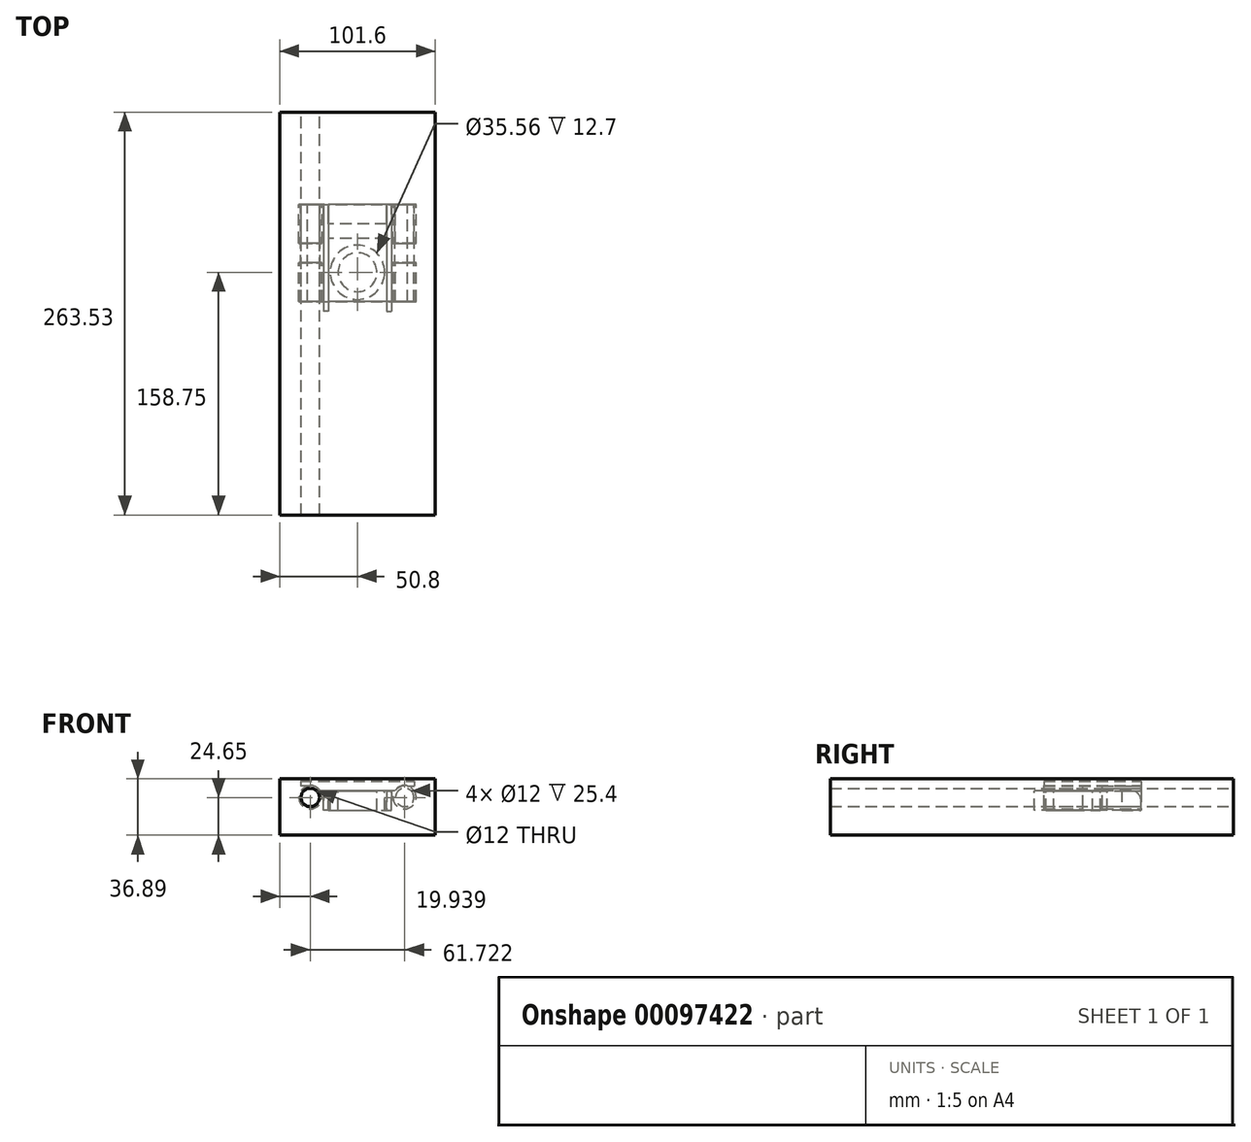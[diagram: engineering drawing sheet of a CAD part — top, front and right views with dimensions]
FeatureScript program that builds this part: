
annotation { "Feature Type Name" : "Feature", "Feature Type Description" : "" }
export const myFeature = defineFeature(function(context is Context, id is Id, definition is map)
    precondition{}
    {
        {
            var Q0;
            Q0=qCreatedBy(makeId("Front.planeOp"),FACE);
            var sketch = newSketch(context, id + "F0", { "sketchPlane" : qUnion([Q0])});
            skCircle(sketch, "E0", {"center": v(30.86, 0) * mm, "radius": 6 * mm});
            skCircle(sketch, "E1.MirrorC", {"center": v(-30.86, 0) * mm, "radius": 6 * mm});
            skLineSegment(sketch, "E2.bottom", {"start": v(50.8, -24.65) * mm, "end": v(-50.8, -24.65) * mm});
            skLineSegment(sketch, "E2.top", {"start": v(50.8, 12.24) * mm, "end": v(-50.8, 12.24) * mm});
            skLineSegment(sketch, "E2.left", {"start": v(50.8, -24.65) * mm, "end": v(50.8, 12.24) * mm});
            skLineSegment(sketch, "E2.right", {"start": v(-50.8, -24.65) * mm, "end": v(-50.8, 12.24) * mm});
            skPoint(sketch, "E2.middle", {"position": v(0, 0) * mm});
            skSolve(sketch);
        }
        {
            var Q0;
            Q0=makeQuery(id+"F0.imprint","IMPRINT",FACE,{"disambiguationData":[TD([[makeQuery(id+"F0.imprint","IMPRINT",EDGE,{"derivedFrom":sQuery(id+"F0.wireOp",EDGE,"E0")}),1.0]])]});
            var Q1;
            Q1=makeQuery(id+"F0.imprint","IMPRINT",FACE,{"disambiguationData":[TD([[makeQuery(id+"F0.imprint","IMPRINT",EDGE,{"derivedFrom":sQuery(id+"F0.wireOp",EDGE,"E1.MirrorC")}),-1.0]])]});
            extrude(context, id + "F1", {"entities" : qUnion([Q0, Q1]), "depth" : 254 * mm});
        }
        {
            var Q0;
            Q0=makeQuery(id+"F0.imprint","IMPRINT",FACE,{"disambiguationData":[TD([[makeQuery(id+"F0.imprint","IMPRINT",EDGE,{"derivedFrom":sQuery(id+"F0.wireOp",EDGE,"E0")}),-1.0]])]});
            var Q1;
            Q1=makeQuery(id+"F0.imprint","IMPRINT",FACE,{"disambiguationData":[TD([[makeQuery(id+"F0.imprint","IMPRINT",EDGE,{"derivedFrom":sQuery(id+"F0.wireOp",EDGE,"E0")}),1.0]])]});
            var Q2;
            Q2=makeQuery(id+"F0.imprint","IMPRINT",FACE,{"disambiguationData":[TD([[makeQuery(id+"F0.imprint","IMPRINT",EDGE,{"derivedFrom":sQuery(id+"F0.wireOp",EDGE,"E1.MirrorC")}),-1.0]])]});
            extrude(context, id + "F2", {"entities" : qUnion([Q0, Q1, Q2]), "operationType" : NewBodyOperationType.ADD, "oppositeDirection" : true, "depth" : 9.52 * mm});
        }
        {
            var Q0;
            Q0=qCreatedBy(makeId("Front.planeOp"),FACE);
            cPlane(context, id + "F3", {"entities" : qUnion([Q0]), "cplaneType" : CPlaneType.OFFSET, "offset" : 50.8 * mm, "width" : 152.4 * mm, "height" : 152.4 * mm});
        }
        {
            var Q0;
            Q0=qCreatedBy(id+"F3.planeOp",FACE);
            var sketch = newSketch(context, id + "F4", { "sketchPlane" : qUnion([Q0])});
            skCircle(sketch, "E3", {"center": v(30.83, 0) * mm, "radius": 7.53 * mm});
            skCircle(sketch, "E4.0", {"center": v(30.86, 0) * mm, "radius": 6 * mm});
            skSolve(sketch);
        }
        {
            var Q0;
            Q0 = qSketchRegion(id + "F4", true);
            extrude(context, id + "F5", {"entities" : qUnion([Q0]), "depth" : 25.4 * mm});
        }
        {
            var Q0;
            Q0=makeQuery(id+"F5.opExtrude","SWEPT_BODY",BODY,{"disambiguationData":[OSD([sQuery(id+"F4.wireOp",EDGE,"E3"),sQuery(id+"F4.wireOp",EDGE,"E4.0")])]});
            var Q1;
            Q1=qCreatedBy(makeId("Right.planeOp"),FACE);
            mirror(context, id + "F6", {"entities" : qUnion([Q0]), "mirrorPlane" : qUnion([Q1])});
        }
        {
            var Q0;
            Q0=makeQuery(id+"F6.opPattern","COPY",BODY,{"derivedFrom":makeQuery(id+"F5.opExtrude","SWEPT_BODY",BODY,{"disambiguationData":[OSD([sQuery(id+"F4.wireOp",EDGE,"E3"),sQuery(id+"F4.wireOp",EDGE,"E4.0")])]}),"instanceName":"1"});
            var Q1;
            Q1=makeQuery(id+"F5.opExtrude","SWEPT_BODY",BODY,{"disambiguationData":[OSD([sQuery(id+"F4.wireOp",EDGE,"E3"),sQuery(id+"F4.wireOp",EDGE,"E4.0")])]});
            var Q2;
            Q2=makeQuery(id+"F0.imprint","IMPRINT",FACE,{"disambiguationData":[TD([[makeQuery(id+"F0.imprint","IMPRINT",EDGE,{"derivedFrom":sQuery(id+"F0.wireOp",EDGE,"E0")}),-1.0]])]});
            transform(context, id + "F7", {"entities" : qUnion([Q0, Q1]), "transformType" : TransformType.TRANSLATION_DISTANCE, "transformDirection" : qUnion([Q2]), "distance" : 38.1 * mm, "makeCopy" : true});
        }
        {
            var Q0;
            Q0=makeQuery(id+"F5.opExtrude","CAP_FACE",FACE,{"disambiguationData":[OSD([sQuery(id+"F4.wireOp",EDGE,"E3"),sQuery(id+"F4.wireOp",EDGE,"E4.0")])],"isStart":true});
            var sketch = newSketch(context, id + "F8", { "sketchPlane" : qUnion([Q0])});
            skCircle(sketch, "E5.0", {"center": v(30.83, 0) * mm, "radius": 7.53 * mm});
            skCircle(sketch, "E6.0", {"center": v(-30.83, 0) * mm, "radius": 7.53 * mm});
            skLineSegment(sketch, "E7", {"start": v(-24.68, 4.36) * mm, "end": v(24.68, 4.36) * mm});
            skLineSegment(sketch, "E8", {"start": v(30.83, 7.53) * mm, "end": v(30.83, 10.7) * mm});
            skLineSegment(sketch, "E9.MirrorCS", {"start": v(-30.83, 7.53) * mm, "end": v(-30.83, 10.7) * mm});
            skLineSegment(sketch, "E10", {"start": v(30.83, 10.7) * mm, "end": v(-30.83, 10.7) * mm});
            skLineSegment(sketch, "E11", {"start": v(-19.05, 4.36) * mm, "end": v(-19.05, -8.34) * mm});
            skLineSegment(sketch, "E12.MirrorCS", {"start": v(19.05, 4.36) * mm, "end": v(19.05, -8.34) * mm});
            skLineSegment(sketch, "E13", {"start": v(19.05, -8.34) * mm, "end": v(-19.05, -8.34) * mm});
            skLineSegment(sketch, "E14.bottom", {"start": v(30.83, 10.7) * mm, "end": v(37.18, 10.7) * mm});
            skLineSegment(sketch, "E14.top", {"start": v(30.83, 7.53) * mm, "end": v(37.18, 7.53) * mm});
            skLineSegment(sketch, "E14.left", {"start": v(30.83, 10.7) * mm, "end": v(30.83, 7.53) * mm});
            skLineSegment(sketch, "E14.right", {"start": v(37.18, 10.7) * mm, "end": v(37.18, 7.53) * mm});
            skLineSegment(sketch, "E15.MirrorCS", {"start": v(-37.18, 10.7) * mm, "end": v(-37.18, 7.53) * mm});
            skLineSegment(sketch, "E16.MirrorCS", {"start": v(-30.83, 10.7) * mm, "end": v(-37.18, 10.7) * mm});
            skLineSegment(sketch, "E17.MirrorCS", {"start": v(-30.83, 7.53) * mm, "end": v(-37.18, 7.53) * mm});
            skCircle(sketch, "E18.0", {"center": v(30.83, 0) * mm, "radius": 7.79 * mm});
            skLineSegment(sketch, "E19.0", {"start": v(-57.15, -31) * mm, "end": v(57.15, -31) * mm});
            skLineSegment(sketch, "E19.1", {"start": v(-57.15, 18.6) * mm, "end": v(-57.15, -31) * mm});
            skLineSegment(sketch, "E19.2", {"start": v(57.15, 18.6) * mm, "end": v(-57.15, 18.6) * mm});
            skLineSegment(sketch, "E19.3", {"start": v(57.15, -31) * mm, "end": v(57.15, 18.6) * mm});
            skCircle(sketch, "E20.MirrorC", {"center": v(-30.83, 0) * mm, "radius": 7.79 * mm});
            skSolve(sketch);
        }
        {
            var Q0;
            {var subQ0=sQuery(id+"F8.wireOp",EDGE,"E11");Q0=makeQuery(id+"F8.imprint","IMPRINT",FACE,{"disambiguationData":[TD([[makeQuery(id+"F8.imprint","IMPRINT",EDGE,{"derivedFrom":subQ0}),1.0]])]});}
            var Q1;
            Q1=makeQuery(id+"F6.opPattern","COPY",FACE,{"derivedFrom":makeQuery(id+"F5.opExtrude","CAP_FACE",FACE,{"disambiguationData":[OSD([sQuery(id+"F4.wireOp",EDGE,"E3"),sQuery(id+"F4.wireOp",EDGE,"E4.0")])],"isStart":false}),"instanceName":"1"});
            extrude(context, id + "F9", {"entities" : qUnion([Q0]), "oppositeDirection" : true, "endBoundEntityFace" : qUnion([Q1]), "depth" : 12.7 * mm});
        }
        {
            var Q0;
            {var subQ0=sQuery(id+"F8.wireOp",EDGE,"E10");Q0=makeQuery(id+"F8.imprint","IMPRINT",FACE,{"disambiguationData":[TD([[makeQuery(id+"F8.imprint","IMPRINT",EDGE,{"derivedFrom":subQ0}),1.0]])]});}
            var Q1;
            {var subQ2=sQuery(id+"F8.wireOp",EDGE,"E14.bottom");Q1=makeQuery(id+"F8.imprint","IMPRINT",FACE,{"disambiguationData":[TD([[makeQuery(id+"F8.imprint","IMPRINT",EDGE,{"derivedFrom":subQ2}),-1.0]])]});}
            var Q2;
            {var subQ1=sQuery(id+"F8.wireOp",EDGE,"E15.MirrorCS");Q2=makeQuery(id+"F8.imprint","IMPRINT",FACE,{"disambiguationData":[TD([[makeQuery(id+"F8.imprint","IMPRINT",EDGE,{"derivedFrom":subQ1}),1.0]])]});}
            var Q3;
            Q3=makeQuery(id+"F7.opPattern","COPY",FACE,{"derivedFrom":makeQuery(id+"F6.opPattern","COPY",FACE,{"derivedFrom":makeQuery(id+"F5.opExtrude","CAP_FACE",FACE,{"disambiguationData":[OSD([sQuery(id+"F4.wireOp",EDGE,"E3"),sQuery(id+"F4.wireOp",EDGE,"E4.0")])],"isStart":false}),"instanceName":"1"}),"instanceName":"1"});
            extrude(context, id + "F10", {"entities" : qUnion([Q0, Q1, Q2]), "endBound" : BoundingType.UP_TO_SURFACE, "oppositeDirection" : true, "endBoundEntityFace" : qUnion([Q3]), "depth" : 25.4 * mm});
        }
        {
            var Q0;
            Q0=makeQuery(id+"F2.opExtrude","SWEPT_FACE",FACE,{"disambiguationData":[OSD([sQuery(id+"F0.wireOp",EDGE,"E2.right")])]});
            var sketch = newSketch(context, id + "F11", { "sketchPlane" : qUnion([Q0])});
            skLineSegment(sketch, "E21.bottom", {"start": v(0, -24.65) * mm, "end": v(254, -24.65) * mm});
            skLineSegment(sketch, "E21.top", {"start": v(0, -31) * mm, "end": v(254, -31) * mm});
            skLineSegment(sketch, "E21.left", {"start": v(0, -24.65) * mm, "end": v(0, -31) * mm});
            skLineSegment(sketch, "E21.right", {"start": v(254, -24.65) * mm, "end": v(254, -31) * mm});
            skSolve(sketch);
        }
        {
            var Q0;
            Q0=makeQuery(id+"F11.imprint","IMPRINT",FACE,{"disambiguationData":[TD([[makeQuery(id+"F11.imprint","IMPRINT",EDGE,{"derivedFrom":sQuery(id+"F11.wireOp",EDGE,"E21.bottom")}),-1.0]])]});
            var Q1;
            Q1=makeQuery(id+"F2.opExtrude","SWEPT_FACE",FACE,{"disambiguationData":[OSD([sQuery(id+"F0.wireOp",EDGE,"E2.left")])]});
            extrude(context, id + "F12", {"entities" : qUnion([Q0]), "endBound" : BoundingType.UP_TO_SURFACE, "oppositeDirection" : true, "endBoundEntityFace" : qUnion([Q1]), "depth" : 25.4 * mm});
        }
        {
            var Q0;
            Q0=makeQuery(id+"F10.opExtrude","SWEPT_FACE",FACE,{"disambiguationData":[OSD([sQuery(id+"F8.wireOp",EDGE,"E7")])]});
            var sketch = newSketch(context, id + "F13", { "sketchPlane" : qUnion([Q0])});
            skCircle(sketch, "E22", {"center": v(0, 95.25) * mm, "radius": 12.7 * mm});
            skLineSegment(sketch, "E23.bottom", {"start": v(19.05, 50.8) * mm, "end": v(22.22, 50.8) * mm});
            skLineSegment(sketch, "E23.top", {"start": v(19.05, 120.65) * mm, "end": v(22.22, 120.65) * mm});
            skLineSegment(sketch, "E23.left", {"start": v(19.05, 50.8) * mm, "end": v(19.05, 120.65) * mm});
            skLineSegment(sketch, "E23.right", {"start": v(22.23, 50.8) * mm, "end": v(22.22, 120.65) * mm});
            skLineSegment(sketch, "E24.bottom", {"start": v(19.05, 73.03) * mm, "end": v(-19.05, 73.03) * mm});
            skLineSegment(sketch, "E24.top", {"start": v(19.05, 117.48) * mm, "end": v(-19.05, 117.48) * mm});
            skLineSegment(sketch, "E24.left", {"start": v(19.05, 73.03) * mm, "end": v(19.05, 117.48) * mm});
            skLineSegment(sketch, "E24.right", {"start": v(-19.05, 73.03) * mm, "end": v(-19.05, 117.48) * mm});
            skLineSegment(sketch, "E25.bottom", {"start": v(-19.05, 117.48) * mm, "end": v(19.05, 117.48) * mm});
            skLineSegment(sketch, "E25.left", {"start": v(-19.05, 117.48) * mm, "end": v(-19.05, 121.92) * mm});
            skLineSegment(sketch, "E25.right", {"start": v(19.05, 117.48) * mm, "end": v(19.05, 120.65) * mm});
            skCircle(sketch, "E26", {"center": v(0, 95.25) * mm, "radius": 17.78 * mm});
            skCircle(sketch, "E27", {"center": v(-10.16, 121.92) * mm, "radius": 5.72 * mm});
            skArc(sketch, "E28.0", {"start": v(-1.38, 123.32) * mm, "mid": v(-10.86, 130.78) * mm, "end": v(-19.05, 121.92) * mm});
            skLineSegment(sketch, "E29.trimOffspring", {"start": v(1.75, 120.65) * mm, "end": v(19.05, 120.65) * mm});
            skPoint(sketch, "E30.visualSharp", {"position": v(-1.36, 120.65) * mm});
            skArc(sketch, "E30.filletArc", {"start": v(-1.38, 123.32) * mm, "mid": v(-0.3, 121.4) * mm, "end": v(1.75, 120.65) * mm});
            skSolve(sketch);
        }
        {
            var Q0;
            Q0=makeQuery(id+"F13.imprint","IMPRINT",FACE,{"disambiguationData":[TD([[makeQuery(id+"F13.imprint","IMPRINT",EDGE,{"derivedFrom":sQuery(id+"F13.wireOp",EDGE,"E22")}),1.0]])]});
            extrude(context, id + "F14", {"entities" : qUnion([Q0]), "depth" : 12.7 * mm});
        }
        {
            var Q0;
            {var subQ4=sQuery(id+"F13.wireOp",EDGE,"E23.bottom");Q0=makeQuery(id+"F13.imprint","IMPRINT",FACE,{"disambiguationData":[TD([[makeQuery(id+"F13.imprint","IMPRINT",EDGE,{"derivedFrom":subQ4}),1.0]])]});}
            var Q1;
            {var subQ0=sQuery(id+"F13.wireOp",EDGE,"E23.top");Q1=makeQuery(id+"F13.imprint","IMPRINT",FACE,{"disambiguationData":[TD([[makeQuery(id+"F13.imprint","IMPRINT",EDGE,{"derivedFrom":subQ0}),-1.0]])]});}
            var Q2;
            {var subQ1=sQuery(id+"F13.wireOp",EDGE,"E23.bottom");Q2=makeQuery(id+"F13.imprint","IMPRINT",FACE,{"disambiguationData":[TD([[makeQuery(id+"F13.imprint","IMPRINT",EDGE,{"derivedFrom":subQ1}),-1.0]])]});}
            extrude(context, id + "F15", {"entities" : qUnion([Q0, Q1, Q2]), "depth" : 12.7 * mm});
        }
        {
            var Q0;
            Q0=makeQuery(id+"F15.opExtrude","CAP_EDGE",EDGE,{"disambiguationData":[OSD([sQuery(id+"F13.wireOp",EDGE,"E23.bottom")])],"isStart":true});
            fillet(context, id + "F16", {"entities" : qUnion([Q0]), "radius" : 6.35 * mm, "tangentPropagation" : true, "allowEdgeOverflow" : false});
        }
        {
            var Q0;
            Q0=makeQuery(id+"F15.opExtrude","SWEPT_BODY",BODY,{"disambiguationData":[OSD([sQuery(id+"F8.wireOp",EDGE,"E7"),sQuery(id+"F13.wireOp",EDGE,"E23.bottom"),sQuery(id+"F13.wireOp",EDGE,"E23.left"),sQuery(id+"F13.wireOp",EDGE,"E23.right")])]});
            var Q1;
            Q1=qCreatedBy(makeId("Right.planeOp"),FACE);
            mirror(context, id + "F17", {"entities" : qUnion([Q0]), "mirrorPlane" : qUnion([Q1])});
        }
        {
            var Q0;
            Q0=makeQuery(id+"F13.imprint","IMPRINT",FACE,{"disambiguationData":[TD([[makeQuery(id+"F13.imprint","IMPRINT",EDGE,{"derivedFrom":sQuery(id+"F13.wireOp",EDGE,"E25.bottom")}),1.0]])]});
            var Q1;
            {var subQ0=sQuery(id+"F13.wireOp",EDGE,"E25.bottom");Q1=makeQuery(id+"F13.imprint","IMPRINT",FACE,{"disambiguationData":[TD([[makeQuery(id+"F13.imprint","IMPRINT",EDGE,{"derivedFrom":subQ0}),-1.0]])]});}
            var Q2;
            {var subQ1=sQuery(id+"F13.wireOp",EDGE,"E24.bottom");Q2=makeQuery(id+"F13.imprint","IMPRINT",FACE,{"disambiguationData":[TD([[makeQuery(id+"F13.imprint","IMPRINT",EDGE,{"derivedFrom":subQ1}),-1.0]])]});}
            var Q3;
            Q3=makeQuery(id+"F17.opPattern","COPY",FACE,{"derivedFrom":makeQuery(id+"F15.opExtrude","CAP_FACE",FACE,{"disambiguationData":[OSD([sQuery(id+"F13.wireOp",EDGE,"E23.bottom"),sQuery(id+"F13.wireOp",EDGE,"E23.top"),sQuery(id+"F13.wireOp",EDGE,"E23.left"),sQuery(id+"F13.wireOp",EDGE,"E23.right"),sQuery(id+"F13.wireOp",EDGE,"E24.left"),sQuery(id+"F13.wireOp",EDGE,"E25.right")])],"isStart":false}),"instanceName":"1"});
            extrude(context, id + "F18", {"entities" : qUnion([Q0, Q1, Q2]), "endBound" : BoundingType.UP_TO_SURFACE, "endBoundEntityFace" : qUnion([Q3]), "depth" : 25.4 * mm});
        }
    });
